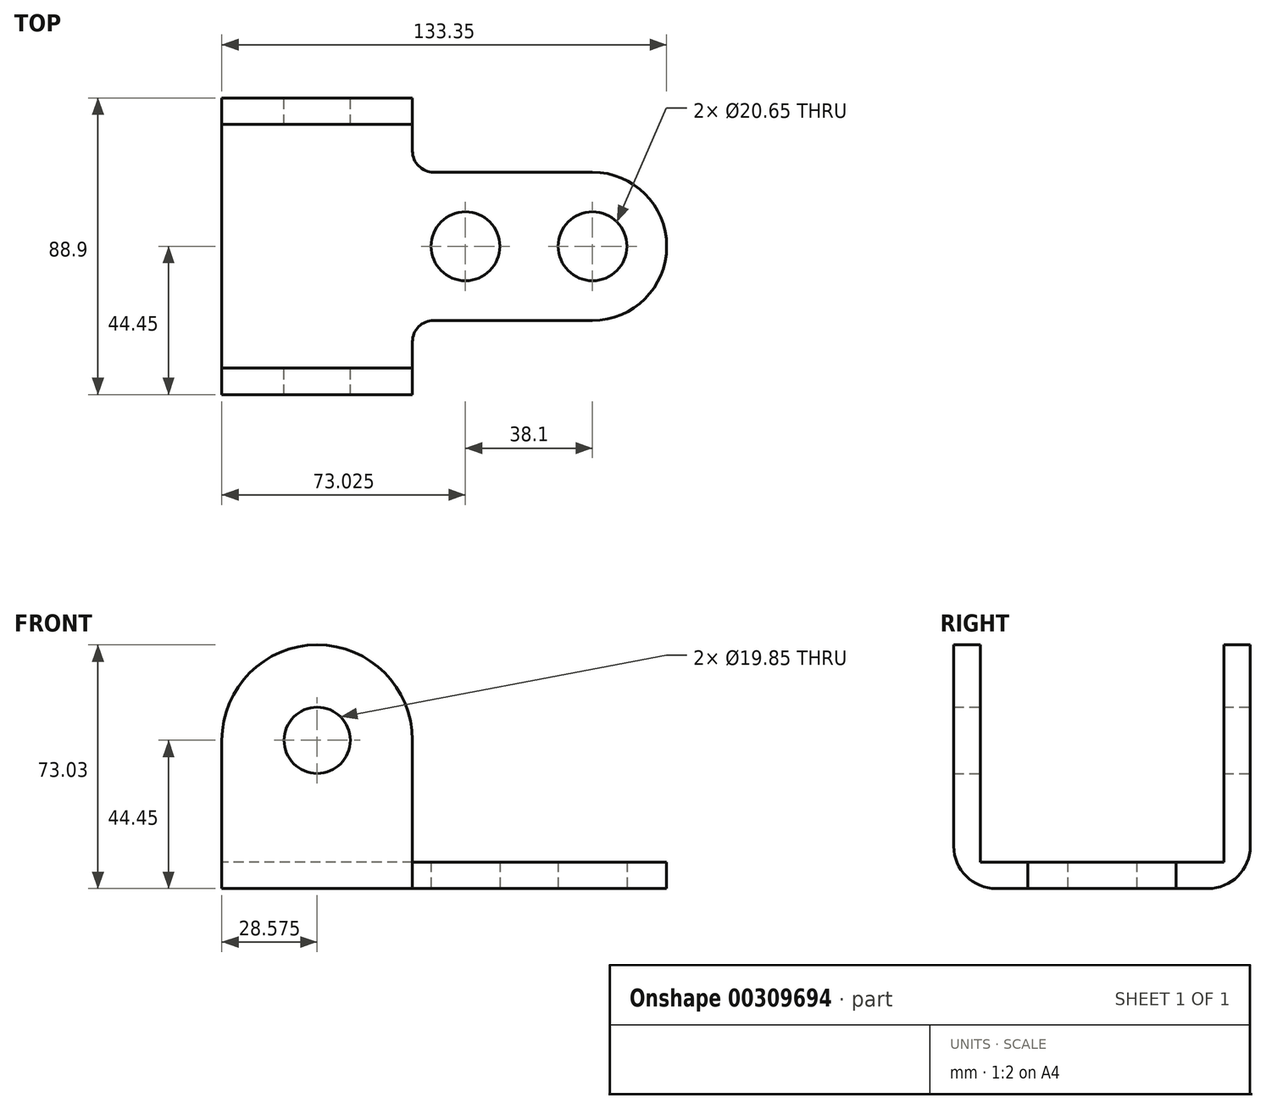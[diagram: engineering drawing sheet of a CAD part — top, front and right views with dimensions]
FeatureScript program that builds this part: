
annotation { "Feature Type Name" : "Feature", "Feature Type Description" : "" }
export const myFeature = defineFeature(function(context is Context, id is Id, definition is map)
    precondition{}
    {
        {
            var Q0;
            Q0=qCreatedBy(makeId("Top.planeOp"),FACE);
            var sketch = newSketch(context, id + "F0", { "sketchPlane" : qUnion([Q0])});
            skLineSegment(sketch, "E0", {"start": v(0, 44.45) * mm, "end": v(0, -44.45) * mm});
            skLineSegment(sketch, "E1", {"start": v(0, 44.45) * mm, "end": v(57.15, 44.45) * mm});
            skLineSegment(sketch, "E2", {"start": v(0, -44.45) * mm, "end": v(57.15, -44.45) * mm});
            skLineSegment(sketch, "E3", {"start": v(63.5, 22.22) * mm, "end": v(111.13, 22.22) * mm});
            skLineSegment(sketch, "E4", {"start": v(63.5, -22.23) * mm, "end": v(111.13, -22.23) * mm});
            skArc(sketch, "E5", {"start": v(111.13, -22.23) * mm, "mid": v(133.35, 0) * mm, "end": v(111.13, 22.23) * mm});
            skLineSegment(sketch, "E6", {"start": v(57.15, 44.45) * mm, "end": v(57.15, 28.57) * mm});
            skLineSegment(sketch, "E7", {"start": v(57.15, -44.45) * mm, "end": v(57.15, -28.57) * mm});
            skArc(sketch, "E8", {"start": v(63.5, -22.23) * mm, "mid": v(59, -24.08) * mm, "end": v(57.15, -28.57) * mm});
            skArc(sketch, "E9", {"start": v(57.15, 28.57) * mm, "mid": v(59, 24.08) * mm, "end": v(63.5, 22.22) * mm});
            skCircle(sketch, "E10", {"center": v(111.13, 0) * mm, "radius": 10.33 * mm});
            skCircle(sketch, "E11", {"center": v(73.03, 0) * mm, "radius": 10.33 * mm});
            skPoint(sketch, "E12", {"position": v(0, 0) * mm});
            skSolve(sketch);
        }
        {
            var Q0;
            Q0=makeQuery(id+"F0.imprint","IMPRINT",FACE,{"disambiguationData":[TD([[makeQuery(id+"F0.imprint","IMPRINT",EDGE,{"derivedFrom":sQuery(id+"F0.wireOp",EDGE,"E0")}),1.0]])]});
            extrude(context, id + "F1", {"entities" : qUnion([Q0]), "depth" : 7.94 * mm});
        }
        {
            var Q0;
            Q0=qCreatedBy(makeId("Front.planeOp"),FACE);
            var sketch = newSketch(context, id + "F2", { "sketchPlane" : qUnion([Q0])});
            skLineSegment(sketch, "E13", {"start": v(0, 0) * mm, "end": v(0, 44.45) * mm});
            skArc(sketch, "E14", {"start": v(57.15, 44.45) * mm, "mid": v(28.58, 73.03) * mm, "end": v(0, 44.45) * mm});
            skLineSegment(sketch, "E15", {"start": v(0, 0) * mm, "end": v(57.15, 0) * mm});
            skLineSegment(sketch, "E16", {"start": v(57.15, 44.45) * mm, "end": v(57.15, 0) * mm});
            skCircle(sketch, "E17", {"center": v(28.58, 44.45) * mm, "radius": 9.92 * mm});
            skLineSegment(sketch, "E18", {"start": v(0, 7.94) * mm, "end": v(57.15, 7.94) * mm});
            skSolve(sketch);
        }
        {
            var Q0;
            {var subQ1=sQuery(id+"F2.wireOp",EDGE,"E14");Q0=makeQuery(id+"F2.imprint","IMPRINT",FACE,{"disambiguationData":[TD([[makeQuery(id+"F2.imprint","IMPRINT",EDGE,{"derivedFrom":subQ1}),1.0]])]});}
            extrude(context, id + "F3", {"entities" : qUnion([Q0]), "operationType" : NewBodyOperationType.ADD, "endBound" : BoundingType.SYMMETRIC, "depth" : 88.9 * mm});
        }
        {
            var Q0;
            Q0=makeQuery(id+"F3.boolean.opBoolean","MERGE",FACE,{"derivedFrom":[makeQuery(id+"F1.opExtrude","SWEPT_FACE",FACE,{"disambiguationData":[OSD([sQuery(id+"F0.wireOp",EDGE,"E0")])]}),makeQuery(id+"F3.opExtrude","SWEPT_FACE",FACE,{"disambiguationData":[OSD([sQuery(id+"F2.wireOp",EDGE,"E13")])]})]});
            var sketch = newSketch(context, id + "F4", { "sketchPlane" : qUnion([Q0])});
            skLineSegment(sketch, "E19.bottom", {"start": v(-36.51, 7.94) * mm, "end": v(36.51, 7.94) * mm});
            skLineSegment(sketch, "E19.top", {"start": v(-36.51, 86.05) * mm, "end": v(36.51, 86.05) * mm});
            skLineSegment(sketch, "E19.left", {"start": v(-36.51, 7.94) * mm, "end": v(-36.51, 86.05) * mm});
            skLineSegment(sketch, "E19.right", {"start": v(36.51, 7.94) * mm, "end": v(36.51, 86.05) * mm});
            skSolve(sketch);
        }
        {
            var Q0;
            Q0 = qSketchRegion(id + "F4", true);
            extrude(context, id + "F5", {"entities" : qUnion([Q0]), "operationType" : NewBodyOperationType.REMOVE, "endBound" : BoundingType.THROUGH_ALL, "oppositeDirection" : true, "depth" : 25.4 * mm});
        }
        {
            var Q0;
            Q0=makeQuery(id+"F1.opExtrude","CAP_EDGE",EDGE,{"disambiguationData":[OSD([sQuery(id+"F0.wireOp",EDGE,"E2")])],"isStart":true});
            var Q1;
            Q1=makeQuery(id+"F1.opExtrude","CAP_EDGE",EDGE,{"disambiguationData":[OSD([sQuery(id+"F0.wireOp",EDGE,"E1")])],"isStart":true});
            fillet(context, id + "F6", {"entities" : qUnion([Q0, Q1]), "radius" : 12.7 * mm, "tangentPropagation" : true, "allowEdgeOverflow" : false});
        }
    });
